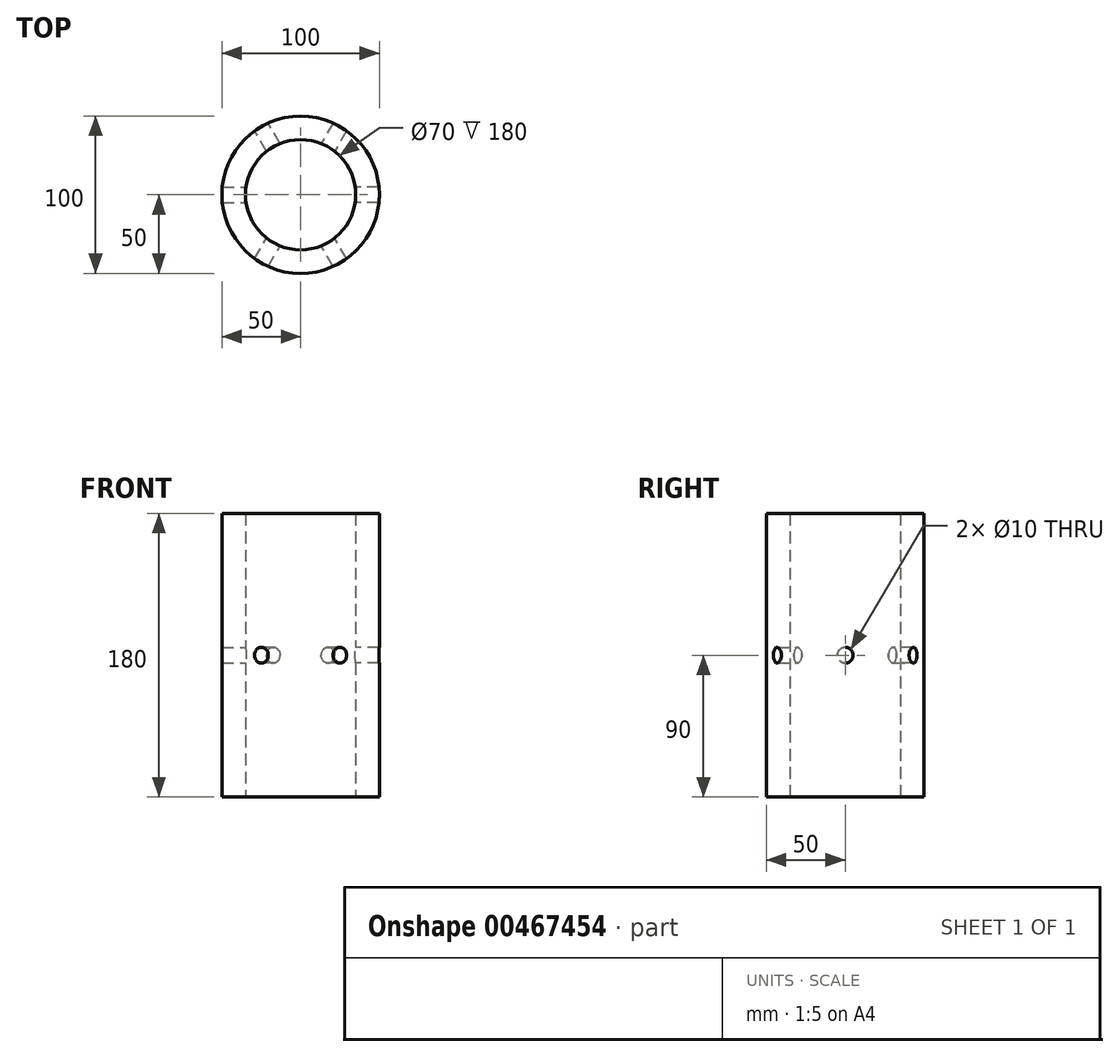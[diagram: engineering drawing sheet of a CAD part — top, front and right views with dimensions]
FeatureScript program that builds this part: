
annotation { "Feature Type Name" : "Feature", "Feature Type Description" : "" }
export const myFeature = defineFeature(function(context is Context, id is Id, definition is map)
    precondition{}
    {
        {
            var Q0;
            Q0=qCreatedBy(makeId("Top.planeOp"),FACE);
            var sketch = newSketch(context, id + "F0", { "sketchPlane" : qUnion([Q0])});
            skCircle(sketch, "E0", {"center": v(0, 0) * mm, "radius": 50 * mm});
            skCircle(sketch, "E1", {"center": v(0, 0) * mm, "radius": 35 * mm});
            skSolve(sketch);
        }
        {
            var Q0;
            Q0=makeQuery(id+"F0.imprint","IMPRINT",FACE,{"disambiguationData":[TD([[makeQuery(id+"F0.imprint","IMPRINT",EDGE,{"derivedFrom":sQuery(id+"F0.wireOp",EDGE,"E0")}),1.0]])]});
            extrude(context, id + "F1", {"entities" : qUnion([Q0]), "depth" : 180 * mm});
        }
        {
            var Q0;
            Q0=qCreatedBy(makeId("Right.planeOp"),FACE);
            var sketch = newSketch(context, id + "F2", { "sketchPlane" : qUnion([Q0])});
            skLineSegment(sketch, "E2.0", {"start": v(-50, 0) * mm, "end": v(50, 0) * mm});
            skLineSegment(sketch, "E3.0", {"start": v(-50, 180) * mm, "end": v(50, 180) * mm});
            skLineSegment(sketch, "E4", {"start": v(0, 0) * mm, "end": v(0, 180) * mm, "construction": true});
            skCircle(sketch, "E5", {"center": v(0, 90) * mm, "radius": 5 * mm});
            skSolve(sketch);
        }
        {
            var Q0;
            Q0=makeQuery(id+"F2.imprint","IMPRINT",FACE,{"disambiguationData":[TD([[makeQuery(id+"F2.imprint","IMPRINT",EDGE,{"derivedFrom":sQuery(id+"F2.wireOp",EDGE,"E5")}),1.0]])]});
            extrude(context, id + "F3", {"entities" : qUnion([Q0]), "depth" : 60 * mm});
        }
        {
            var Q0;
            Q0=makeQuery(id+"F3.opExtrude","SWEPT_BODY",BODY,{"disambiguationData":[OSD([sQuery(id+"F2.wireOp",EDGE,"E5")])]});
            var Q1;
            Q1=sQuery(id+"F2.wireOp",EDGE,"E4");
            circularPattern(context, id + "F4", {"entities" : qUnion([Q0]), "axis" : qUnion([Q1]), "angle" : 360 * degree, "instanceCount" : 6, "equalSpace" : true});
        }
        {
            var Q0;
            Q0=makeQuery(id+"F4.opPattern","COPY",BODY,{"derivedFrom":makeQuery(id+"F3.opExtrude","SWEPT_BODY",BODY,{"disambiguationData":[OSD([sQuery(id+"F2.wireOp",EDGE,"E5")])]}),"instanceName":"4"});
            var Q1;
            Q1=makeQuery(id+"F4.opPattern","COPY",BODY,{"derivedFrom":makeQuery(id+"F3.opExtrude","SWEPT_BODY",BODY,{"disambiguationData":[OSD([sQuery(id+"F2.wireOp",EDGE,"E5")])]}),"instanceName":"5"});
            var Q2;
            Q2=makeQuery(id+"F3.opExtrude","SWEPT_BODY",BODY,{"disambiguationData":[OSD([sQuery(id+"F2.wireOp",EDGE,"E5")])]});
            var Q3;
            Q3=makeQuery(id+"F4.opPattern","COPY",BODY,{"derivedFrom":makeQuery(id+"F3.opExtrude","SWEPT_BODY",BODY,{"disambiguationData":[OSD([sQuery(id+"F2.wireOp",EDGE,"E5")])]}),"instanceName":"1"});
            var Q4;
            Q4=makeQuery(id+"F4.opPattern","COPY",BODY,{"derivedFrom":makeQuery(id+"F3.opExtrude","SWEPT_BODY",BODY,{"disambiguationData":[OSD([sQuery(id+"F2.wireOp",EDGE,"E5")])]}),"instanceName":"2"});
            var Q5;
            Q5=makeQuery(id+"F4.opPattern","COPY",BODY,{"derivedFrom":makeQuery(id+"F3.opExtrude","SWEPT_BODY",BODY,{"disambiguationData":[OSD([sQuery(id+"F2.wireOp",EDGE,"E5")])]}),"instanceName":"3"});
            var Q6;
            Q6=makeQuery(id+"F1.opExtrude","SWEPT_BODY",BODY,{"disambiguationData":[OSD([sQuery(id+"F0.wireOp",EDGE,"E0"),sQuery(id+"F0.wireOp",EDGE,"E1")])]});
            booleanBodies(context, id + "F5", {"operationType" : BooleanOperationType.SUBTRACTION, "tools" : qUnion([Q0, Q1, Q2, Q3, Q4, Q5]), "targets" : qUnion([Q6])});
        }
    });
